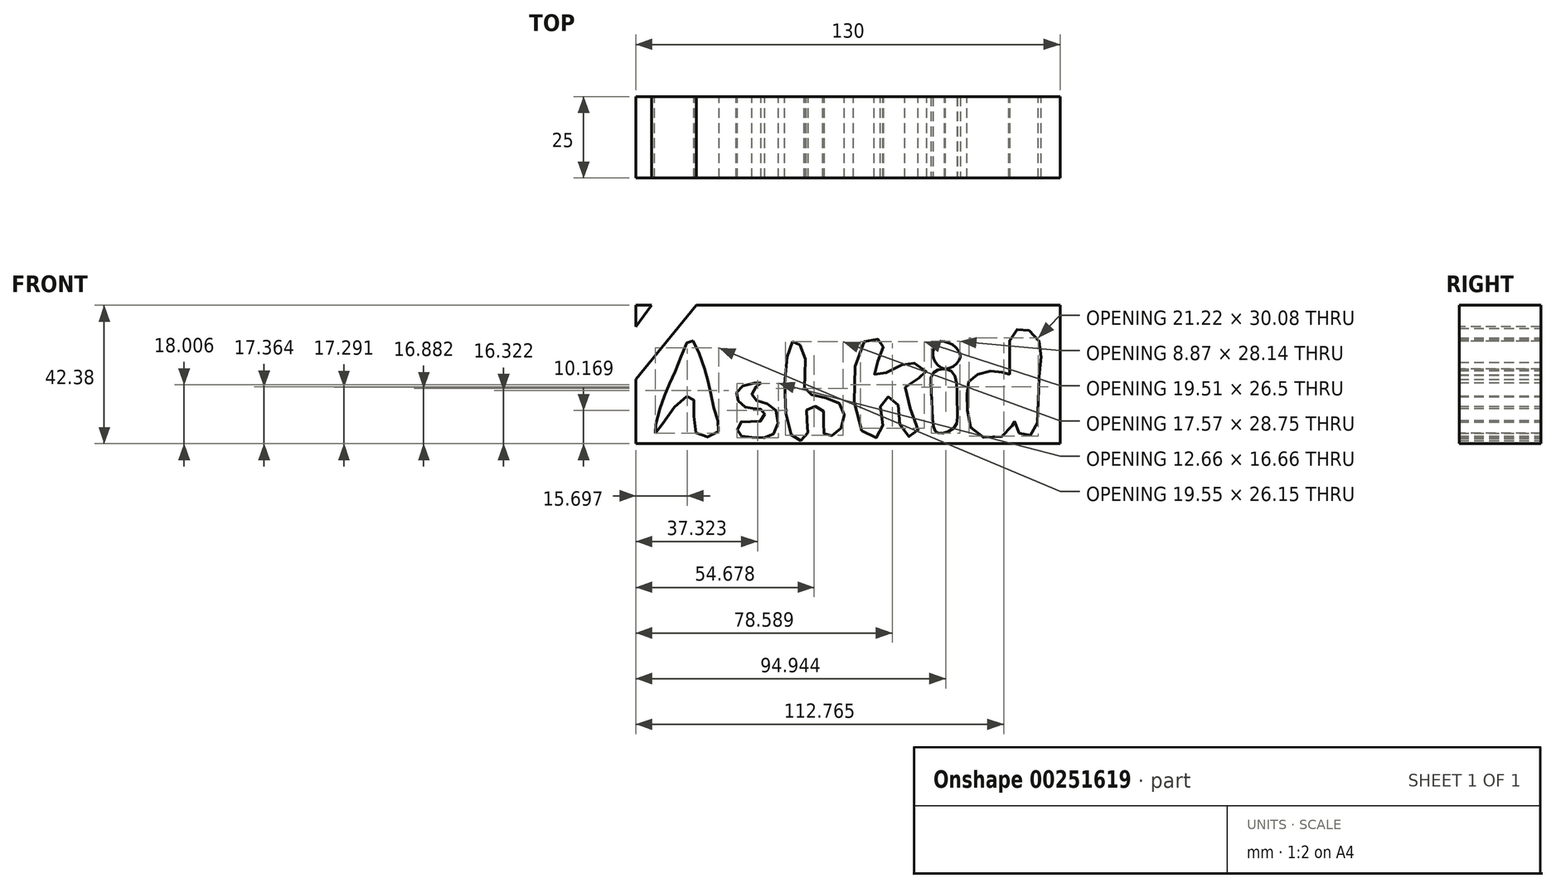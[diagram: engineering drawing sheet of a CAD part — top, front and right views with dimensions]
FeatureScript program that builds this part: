
annotation { "Feature Type Name" : "Feature", "Feature Type Description" : "" }
export const myFeature = defineFeature(function(context is Context, id is Id, definition is map)
    precondition{}
    {
        {
            var Q0;
            Q0=qCreatedBy(makeId("Front.planeOp"),FACE);
            var sketch = newSketch(context, id + "F0", { "sketchPlane" : qUnion([Q0])});
            skLineSegment(sketch, "E0.bottom", {"start": v(-75.35, 21.19) * mm, "end": v(54.65, 21.19) * mm});
            skLineSegment(sketch, "E0.top", {"start": v(-75.35, -21.19) * mm, "end": v(54.65, -21.19) * mm});
            skLineSegment(sketch, "E0.left", {"start": v(-75.35, 21.19) * mm, "end": v(-75.35, -21.19) * mm});
            skPoint(sketch, "E0.middle", {"position": v(0, 0) * mm});
            skFitSpline(sketch, "E1", {"points": [v(-69.43, -17.94) * mm, v(-68.3, -11.66) * mm, v(-65.5, -4) * mm, v(-61.77, 4.6) * mm, v(-58.6, 10.75) * mm, v(-54.86, 3.47) * mm, v(-52.8, -4) * mm, v(-50.75, -12.59) * mm, v(-50.38, -17.82) * mm, v(-56.73, -18.2) * mm, v(-57.66, -7.36) * mm, v(-61.77, -8.1) * mm, v(-69.43, -17.94) * mm]});
            skFitSpline(sketch, "E2", {"points": [v(-36.93, -2.7) * mm, v(-41.42, -3.06) * mm, v(-44.6, -6.24) * mm, v(-41.98, -9.97) * mm, v(-38.62, -10.35) * mm, v(-36, -11.47) * mm, v(-37.5, -14.46) * mm, v(-42.91, -14.46) * mm, v(-44.03, -17.94) * mm, v(-39.18, -19.31) * mm, v(-32.83, -17.94) * mm, v(-33.01, -10.16) * mm, v(-39.18, -7.55) * mm, v(-39.18, -4.37) * mm, v(-36.93, -2.7) * mm]});
            skFitSpline(sketch, "E3", {"points": [v(-27.34, 10.07) * mm, v(-26.96, -19.62) * mm, v(-22.67, -17.94) * mm, v(-22.86, -10.66) * mm, v(-18, -10.85) * mm, v(-17.81, -17.94) * mm, v(-13.7, -17.94) * mm, v(-12.59, -9.17) * mm, v(-22.86, -5.43) * mm, v(-23.42, 4.47) * mm, v(-27.34, 10.07) * mm]});
            skFitSpline(sketch, "E4", {"points": [v(-5.38, 10.07) * mm, v(-5.56, -17.94) * mm, v(0, -17.94) * mm, v(0, -8.1) * mm, v(4.34, -7.73) * mm, v(6.58, -17.94) * mm, v(11.06, -17.94) * mm, v(7.32, -3.63) * mm, v(13.67, 0) * mm, v(10.12, 3.47) * mm, v(4.34, 1.98) * mm, v(-2.2, 0) * mm, v(0, 6.65) * mm, v(0, 10.07) * mm, v(-5.38, 10.07) * mm]});
            skFitSpline(sketch, "E5", {"points": [v(15.99, 0.73) * mm, v(15.24, -5.43) * mm, v(15.99, -16.45) * mm, v(17.48, -17.94) * mm, v(22.34, -16.26) * mm, v(23.08, -9.17) * mm, v(21.59, 0.92) * mm, v(15.99, 0.73) * mm]});
            skFitSpline(sketch, "E6", {"points": [v(17.67, 10.07) * mm, v(15.99, 7.83) * mm, v(15.99, 4.84) * mm, v(19.3, 1.74) * mm, v(23.83, 4.65) * mm, v(22.7, 8.39) * mm, v(17.67, 10.07) * mm]});
            skFitSpline(sketch, "E7", {"points": [v(36.9, 0.73) * mm, v(31.67, 0.73) * mm, v(26.82, -1.94) * mm, v(26.26, -7.92) * mm, v(28.5, -17.94) * mm, v(38.58, -17.94) * mm, v(40.64, -14.08) * mm, v(42.13, -17.94) * mm, v(46.43, -17.94) * mm, v(48.1, -2.5) * mm, v(48.3, 10.07) * mm, v(42.88, 14.12) * mm, v(39.14, 10.07) * mm, v(39.14, 0) * mm, v(36.9, 0.73) * mm]});
            skPoint(sketch, "E8.end.orphan", {"position": v(48.31, 0) * mm});
            skLineSegment(sketch, "E9", {"start": v(54.65, 21.19) * mm, "end": v(54.65, -21.19) * mm});
            skPoint(sketch, "E10.orphan", {"position": v(75.35, -21.19) * mm});
            skPoint(sketch, "E11.orphan", {"position": v(75.35, 21.19) * mm});
            skSolve(sketch);
        }
        {
            var Q0;
            Q0 = qSketchRegion(id + "F0", true);
            extrude(context, id + "F1", {"entities" : qUnion([Q0]), "depth" : 25 * mm});
        }
        {
            var Q0;
            Q0=makeQuery(id+"F1.opExtrude","CAP_FACE",FACE,{"disambiguationData":[OSD([sQuery(id+"F0.wireOp",EDGE,"E0.bottom"),sQuery(id+"F0.wireOp",EDGE,"E0.top"),sQuery(id+"F0.wireOp",EDGE,"E0.left"),sQuery(id+"F0.wireOp",EDGE,"E1"),sQuery(id+"F0.wireOp",EDGE,"E2"),sQuery(id+"F0.wireOp",EDGE,"E3"),sQuery(id+"F0.wireOp",EDGE,"E4"),sQuery(id+"F0.wireOp",EDGE,"E5"),sQuery(id+"F0.wireOp",EDGE,"E6"),sQuery(id+"F0.wireOp",EDGE,"E7"),sQuery(id+"F0.wireOp",EDGE,"E9")])],"isStart":false});
            var sketch = newSketch(context, id + "F2", { "sketchPlane" : qUnion([Q0])});
            skLineSegment(sketch, "E12", {"start": v(-62.41, 32.12) * mm, "end": v(-89.09, -4) * mm});
            skLineSegment(sketch, "E13", {"start": v(-89.09, -4) * mm, "end": v(-81.79, -9.38) * mm});
            skLineSegment(sketch, "E14", {"start": v(-81.79, -9.38) * mm, "end": v(-50.8, 28.49) * mm});
            skLineSegment(sketch, "E15", {"start": v(-50.8, 28.49) * mm, "end": v(-62.41, 32.12) * mm});
            skSolve(sketch);
        }
        {
            var Q0;
            Q0 = qSketchRegion(id + "F2", true);
            extrude(context, id + "F3", {"entities" : qUnion([Q0]), "operationType" : NewBodyOperationType.REMOVE, "oppositeDirection" : true, "depth" : 25 * mm});
        }
    });
